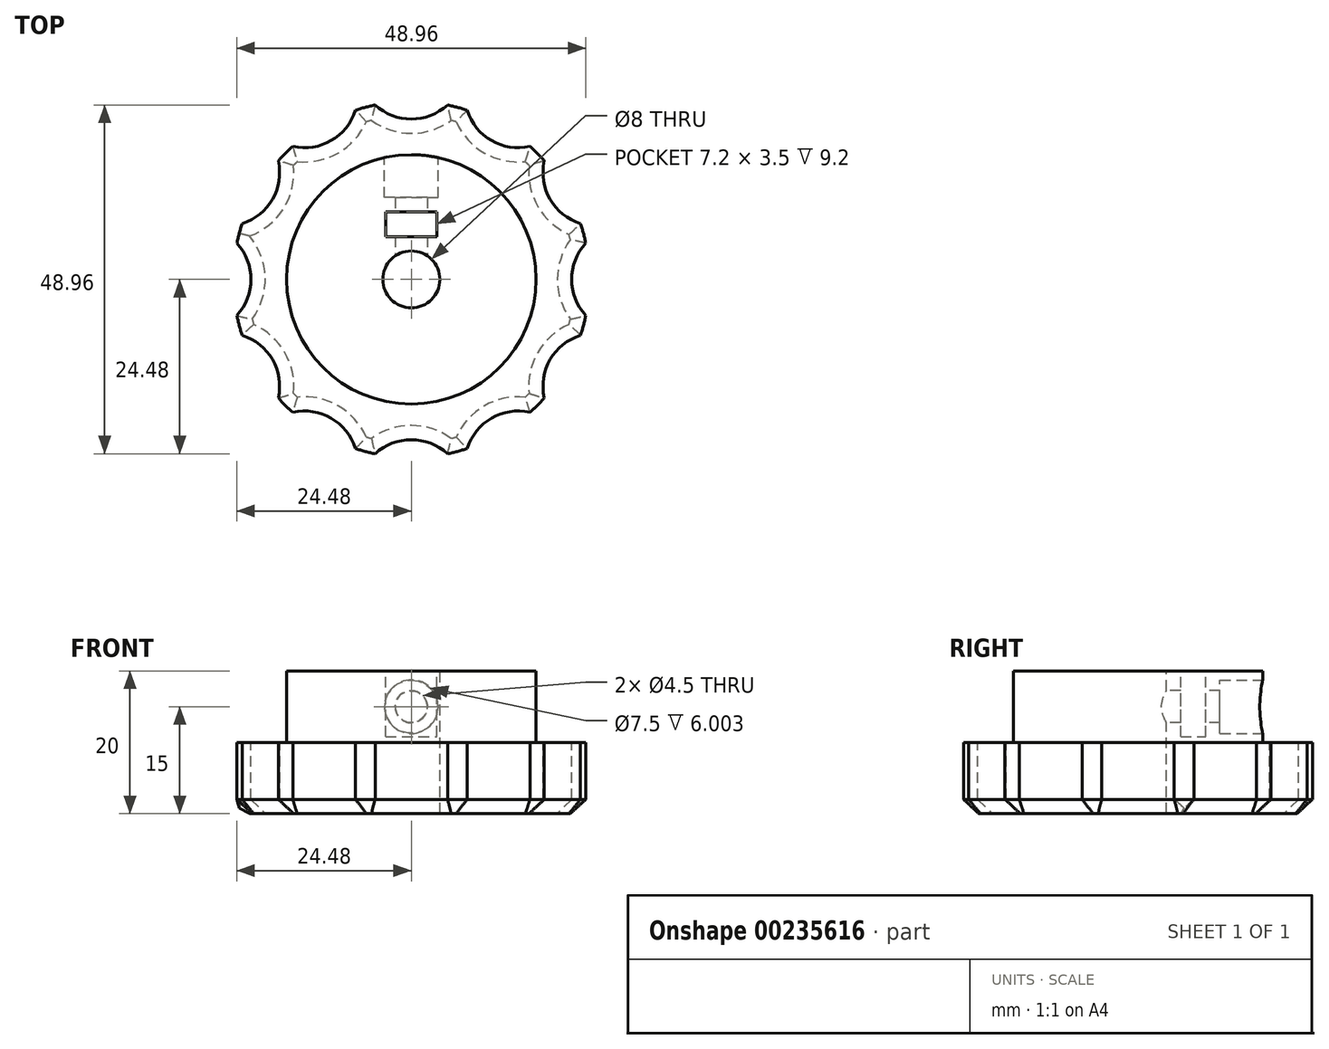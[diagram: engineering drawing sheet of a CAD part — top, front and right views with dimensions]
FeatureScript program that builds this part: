
annotation { "Feature Type Name" : "Feature", "Feature Type Description" : "" }
export const myFeature = defineFeature(function(context is Context, id is Id, definition is map)
    precondition{}
    {
        {
            var Q0;
            Q0=qCreatedBy(makeId("Top.planeOp"),FACE);
            var sketch = newSketch(context, id + "F0", { "sketchPlane" : qUnion([Q0])});
            skCircle(sketch, "E0", {"center": v(0, 0) * mm, "radius": 25 * mm});
            skSolve(sketch);
        }
        {
            var Q0;
            Q0 = qSketchRegion(id + "F0", true);
            extrude(context, id + "F1", {"entities" : qUnion([Q0]), "depth" : 10 * mm, "offsetDistance" : 25 * mm});
        }
        {
            var Q0;
            Q0=makeQuery(id+"F1.opExtrude","CAP_FACE",FACE,{"disambiguationData":[OSD([sQuery(id+"F0.wireOp",EDGE,"E0")])],"isStart":false});
            var sketch = newSketch(context, id + "F2", { "sketchPlane" : qUnion([Q0])});
            skCircle(sketch, "E1", {"center": v(0, 30) * mm, "radius": 7.5 * mm});
            skCircle(sketch, "E2.1.0", {"center": v(-15, 25.98) * mm, "radius": 7.5 * mm});
            skCircle(sketch, "E2.2.0", {"center": v(-25.98, 15) * mm, "radius": 7.5 * mm});
            skCircle(sketch, "E2.3.0", {"center": v(-30, 0) * mm, "radius": 7.5 * mm});
            skCircle(sketch, "E2.4.0", {"center": v(-25.98, -15) * mm, "radius": 7.5 * mm});
            skCircle(sketch, "E2.5.0", {"center": v(-15, -25.98) * mm, "radius": 7.5 * mm});
            skCircle(sketch, "E2.6.0", {"center": v(0, -30) * mm, "radius": 7.5 * mm});
            skCircle(sketch, "E2.7.0", {"center": v(15, -25.98) * mm, "radius": 7.5 * mm});
            skCircle(sketch, "E2.8.0", {"center": v(25.98, -15) * mm, "radius": 7.5 * mm});
            skCircle(sketch, "E2.9.0", {"center": v(30, 0) * mm, "radius": 7.5 * mm});
            skCircle(sketch, "E2.10.0", {"center": v(25.98, 15) * mm, "radius": 7.5 * mm});
            skCircle(sketch, "E2.11.0", {"center": v(15, 25.98) * mm, "radius": 7.5 * mm});
            skPoint(sketch, "E2.center", {"position": v(0, 0) * mm});
            skSolve(sketch);
        }
        {
            var Q0;
            Q0 = qSketchRegion(id + "F2", true);
            extrude(context, id + "F3", {"entities" : qUnion([Q0]), "operationType" : NewBodyOperationType.REMOVE, "endBound" : BoundingType.THROUGH_ALL, "oppositeDirection" : true, "depth" : 25 * mm, "offsetDistance" : 25 * mm});
        }
        {
            var Q0;
            Q0=makeQuery(id+"F1.opExtrude","CAP_FACE",FACE,{"disambiguationData":[OSD([sQuery(id+"F0.wireOp",EDGE,"E0")])],"isStart":false});
            var sketch = newSketch(context, id + "F4", { "sketchPlane" : qUnion([Q0])});
            skCircle(sketch, "E3", {"center": v(0, 0) * mm, "radius": 17.5 * mm});
            skSolve(sketch);
        }
        {
            var Q0;
            Q0=makeQuery(id+"F4.imprint","IMPRINT",FACE,{"disambiguationData":[TD([[makeQuery(id+"F4.imprint","IMPRINT",EDGE,{"derivedFrom":sQuery(id+"F4.wireOp",EDGE,"E3")}),1.0]])]});
            extrude(context, id + "F5", {"entities" : qUnion([Q0]), "operationType" : NewBodyOperationType.ADD, "depth" : 10 * mm, "offsetDistance" : 25 * mm});
        }
        {
            var Q0;
            Q0=makeQuery(id+"F5.opExtrude","CAP_FACE",FACE,{"disambiguationData":[OSD([sQuery(id+"F4.wireOp",EDGE,"E3")])],"isStart":false});
            var sketch = newSketch(context, id + "F6", { "sketchPlane" : qUnion([Q0])});
            skCircle(sketch, "E4", {"center": v(0, 0) * mm, "radius": 4 * mm});
            skSolve(sketch);
        }
        {
            var Q0;
            Q0 = qSketchRegion(id + "F6", true);
            extrude(context, id + "F7", {"entities" : qUnion([Q0]), "operationType" : NewBodyOperationType.REMOVE, "endBound" : BoundingType.UP_TO_NEXT, "oppositeDirection" : true, "depth" : 25 * mm, "offsetDistance" : 25 * mm});
        }
        {
            var Q0;
            Q0=qCreatedBy(makeId("Front.planeOp"),FACE);
            var sketch = newSketch(context, id + "F8", { "sketchPlane" : qUnion([Q0])});
            skCircle(sketch, "E5", {"center": v(0, 15) * mm, "radius": 2.25 * mm});
            skSolve(sketch);
        }
        {
            var Q0;
            Q0 = qSketchRegion(id + "F8", true);
            extrude(context, id + "F9", {"entities" : qUnion([Q0]), "operationType" : NewBodyOperationType.REMOVE, "endBound" : BoundingType.THROUGH_ALL, "oppositeDirection" : true, "depth" : 25 * mm, "offsetDistance" : 25 * mm});
        }
        {
            var Q0;
            Q0=makeQuery(id+"F5.opExtrude","CAP_FACE",FACE,{"disambiguationData":[OSD([sQuery(id+"F4.wireOp",EDGE,"E3")])],"isStart":false});
            var sketch = newSketch(context, id + "F10", { "sketchPlane" : qUnion([Q0])});
            skLineSegment(sketch, "E6.bottom", {"start": v(-3.6, 6) * mm, "end": v(3.6, 6) * mm});
            skLineSegment(sketch, "E6.top", {"start": v(-3.6, 9.5) * mm, "end": v(3.6, 9.5) * mm});
            skLineSegment(sketch, "E6.left", {"start": v(-3.6, 6) * mm, "end": v(-3.6, 9.5) * mm});
            skLineSegment(sketch, "E6.right", {"start": v(3.6, 6) * mm, "end": v(3.6, 9.5) * mm});
            skSolve(sketch);
        }
        {
            var Q0;
            Q0 = qSketchRegion(id + "F10", true);
            extrude(context, id + "F11", {"entities" : qUnion([Q0]), "operationType" : NewBodyOperationType.REMOVE, "oppositeDirection" : true, "depth" : 9.2 * mm, "offsetDistance" : 25 * mm});
        }
        {
            var Q0;
            Q0=qCreatedBy(makeId("Front.planeOp"),FACE);
            cPlane(context, id + "F12", {"entities" : qUnion([Q0]), "cplaneType" : CPlaneType.OFFSET, "offset" : 25 * mm, "oppositeDirection" : true, "width" : 150 * mm, "height" : 150 * mm});
        }
        {
            var Q0;
            Q0=qCreatedBy(id+"F12.planeOp",FACE);
            var sketch = newSketch(context, id + "F13", { "sketchPlane" : qUnion([Q0])});
            skCircle(sketch, "E7", {"center": v(0, 15) * mm, "radius": 3.75 * mm});
            skSolve(sketch);
        }
        {
            var Q0;
            Q0=makeQuery(id+"F13.imprint","IMPRINT",FACE,{"disambiguationData":[TD([[makeQuery(id+"F13.imprint","IMPRINT",EDGE,{"derivedFrom":sQuery(id+"F13.wireOp",EDGE,"E7")}),1.0]])]});
            var Q1;
            Q1=makeQuery(id+"F11.boolean.opBoolean","COPY",FACE,{"derivedFrom":makeQuery(id+"F11.opExtrude","SWEPT_FACE",FACE,{"disambiguationData":[OSD([sQuery(id+"F10.wireOp",EDGE,"E6.top")])]})});
            extrude(context, id + "F14", {"entities" : qUnion([Q0]), "operationType" : NewBodyOperationType.REMOVE, "endBound" : BoundingType.UP_TO_SURFACE, "depth" : 25 * mm, "endBoundEntityFace" : qUnion([Q1]), "hasOffset" : true, "offsetDistance" : 2 * mm});
        }
        {
            var Q0;
            Q0=makeQuery(id+"F3.boolean.opBoolean","INTERSECT",EDGE,{"derivedFrom":[makeQuery(id+"F1.opExtrude","CAP_FACE",FACE,{"disambiguationData":[OSD([sQuery(id+"F0.wireOp",EDGE,"E0")])],"isStart":true}),makeQuery(id+"F3.opExtrude","SWEPT_FACE",FACE,{"disambiguationData":[OSD([sQuery(id+"F2.wireOp",EDGE,"E2.10.0")])]})]});
            var Q1;
            {var subQ0=sQuery(id+"F0.wireOp",EDGE,"E0");Q1=makeQuery(id+"F3.boolean.opBoolean","SPLIT",EDGE,{"disambiguationData":[TD([makeQuery(id+"F1.opExtrude","SWEPT_FACE",FACE,{"disambiguationData":[OSD([subQ0])]}),makeQuery(id+"F1.opExtrude","CAP_FACE",FACE,{"disambiguationData":[OSD([subQ0])],"isStart":true}),makeQuery(id+"F3.opExtrude","SWEPT_FACE",FACE,{"disambiguationData":[OSD([sQuery(id+"F2.wireOp",EDGE,"E2.10.0")])]}),makeQuery(id+"F3.opExtrude","SWEPT_FACE",FACE,{"disambiguationData":[OSD([sQuery(id+"F2.wireOp",EDGE,"E2.11.0")])]})])],"derivedFrom":makeQuery(id+"F1.opExtrude","CAP_EDGE",EDGE,{"disambiguationData":[OSD([subQ0])],"isStart":true})});}
            var Q2;
            Q2=makeQuery(id+"F3.boolean.opBoolean","INTERSECT",EDGE,{"derivedFrom":[makeQuery(id+"F1.opExtrude","CAP_FACE",FACE,{"disambiguationData":[OSD([sQuery(id+"F0.wireOp",EDGE,"E0")])],"isStart":true}),makeQuery(id+"F3.opExtrude","SWEPT_FACE",FACE,{"disambiguationData":[OSD([sQuery(id+"F2.wireOp",EDGE,"E2.11.0")])]})]});
            var Q3;
            {var subQ0=sQuery(id+"F0.wireOp",EDGE,"E0");Q3=makeQuery(id+"F3.boolean.opBoolean","SPLIT",EDGE,{"disambiguationData":[TD([makeQuery(id+"F1.opExtrude","SWEPT_FACE",FACE,{"disambiguationData":[OSD([subQ0])]}),makeQuery(id+"F1.opExtrude","CAP_FACE",FACE,{"disambiguationData":[OSD([subQ0])],"isStart":true}),makeQuery(id+"F3.opExtrude","SWEPT_FACE",FACE,{"disambiguationData":[OSD([sQuery(id+"F2.wireOp",EDGE,"E1")])]}),makeQuery(id+"F3.opExtrude","SWEPT_FACE",FACE,{"disambiguationData":[OSD([sQuery(id+"F2.wireOp",EDGE,"E2.11.0")])]})])],"derivedFrom":makeQuery(id+"F1.opExtrude","CAP_EDGE",EDGE,{"disambiguationData":[OSD([subQ0])],"isStart":true})});}
            var Q4;
            Q4=makeQuery(id+"F3.boolean.opBoolean","INTERSECT",EDGE,{"derivedFrom":[makeQuery(id+"F1.opExtrude","CAP_FACE",FACE,{"disambiguationData":[OSD([sQuery(id+"F0.wireOp",EDGE,"E0")])],"isStart":true}),makeQuery(id+"F3.opExtrude","SWEPT_FACE",FACE,{"disambiguationData":[OSD([sQuery(id+"F2.wireOp",EDGE,"E1")])]})]});
            var Q5;
            {var subQ0=sQuery(id+"F0.wireOp",EDGE,"E0");Q5=makeQuery(id+"F3.boolean.opBoolean","SPLIT",EDGE,{"disambiguationData":[TD([makeQuery(id+"F1.opExtrude","SWEPT_FACE",FACE,{"disambiguationData":[OSD([subQ0])]}),makeQuery(id+"F1.opExtrude","CAP_FACE",FACE,{"disambiguationData":[OSD([subQ0])],"isStart":true}),makeQuery(id+"F3.opExtrude","SWEPT_FACE",FACE,{"disambiguationData":[OSD([sQuery(id+"F2.wireOp",EDGE,"E1")])]}),makeQuery(id+"F3.opExtrude","SWEPT_FACE",FACE,{"disambiguationData":[OSD([sQuery(id+"F2.wireOp",EDGE,"E2.1.0")])]})])],"derivedFrom":makeQuery(id+"F1.opExtrude","CAP_EDGE",EDGE,{"disambiguationData":[OSD([subQ0])],"isStart":true})});}
            var Q6;
            Q6=makeQuery(id+"F3.boolean.opBoolean","INTERSECT",EDGE,{"derivedFrom":[makeQuery(id+"F1.opExtrude","CAP_FACE",FACE,{"disambiguationData":[OSD([sQuery(id+"F0.wireOp",EDGE,"E0")])],"isStart":true}),makeQuery(id+"F3.opExtrude","SWEPT_FACE",FACE,{"disambiguationData":[OSD([sQuery(id+"F2.wireOp",EDGE,"E2.1.0")])]})]});
            var Q7;
            {var subQ0=sQuery(id+"F0.wireOp",EDGE,"E0");Q7=makeQuery(id+"F3.boolean.opBoolean","SPLIT",EDGE,{"disambiguationData":[TD([makeQuery(id+"F1.opExtrude","SWEPT_FACE",FACE,{"disambiguationData":[OSD([subQ0])]}),makeQuery(id+"F1.opExtrude","CAP_FACE",FACE,{"disambiguationData":[OSD([subQ0])],"isStart":true}),makeQuery(id+"F3.opExtrude","SWEPT_FACE",FACE,{"disambiguationData":[OSD([sQuery(id+"F2.wireOp",EDGE,"E2.1.0")])]}),makeQuery(id+"F3.opExtrude","SWEPT_FACE",FACE,{"disambiguationData":[OSD([sQuery(id+"F2.wireOp",EDGE,"E2.2.0")])]})])],"derivedFrom":makeQuery(id+"F1.opExtrude","CAP_EDGE",EDGE,{"disambiguationData":[OSD([subQ0])],"isStart":true})});}
            var Q8;
            Q8=makeQuery(id+"F3.boolean.opBoolean","INTERSECT",EDGE,{"derivedFrom":[makeQuery(id+"F1.opExtrude","CAP_FACE",FACE,{"disambiguationData":[OSD([sQuery(id+"F0.wireOp",EDGE,"E0")])],"isStart":true}),makeQuery(id+"F3.opExtrude","SWEPT_FACE",FACE,{"disambiguationData":[OSD([sQuery(id+"F2.wireOp",EDGE,"E2.2.0")])]})]});
            var Q9;
            Q9=makeQuery(id+"F3.boolean.opBoolean","INTERSECT",EDGE,{"derivedFrom":[makeQuery(id+"F1.opExtrude","CAP_FACE",FACE,{"disambiguationData":[OSD([sQuery(id+"F0.wireOp",EDGE,"E0")])],"isStart":true}),makeQuery(id+"F3.opExtrude","SWEPT_FACE",FACE,{"disambiguationData":[OSD([sQuery(id+"F2.wireOp",EDGE,"E2.3.0")])]})]});
            var Q10;
            {var subQ0=sQuery(id+"F0.wireOp",EDGE,"E0");Q10=makeQuery(id+"F3.boolean.opBoolean","SPLIT",EDGE,{"disambiguationData":[TD([makeQuery(id+"F1.opExtrude","SWEPT_FACE",FACE,{"disambiguationData":[OSD([subQ0])]}),makeQuery(id+"F1.opExtrude","CAP_FACE",FACE,{"disambiguationData":[OSD([subQ0])],"isStart":true}),makeQuery(id+"F3.opExtrude","SWEPT_FACE",FACE,{"disambiguationData":[OSD([sQuery(id+"F2.wireOp",EDGE,"E2.3.0")])]}),makeQuery(id+"F3.opExtrude","SWEPT_FACE",FACE,{"disambiguationData":[OSD([sQuery(id+"F2.wireOp",EDGE,"E2.4.0")])]})])],"derivedFrom":makeQuery(id+"F1.opExtrude","CAP_EDGE",EDGE,{"disambiguationData":[OSD([subQ0])],"isStart":true})});}
            var Q11;
            Q11=makeQuery(id+"F3.boolean.opBoolean","INTERSECT",EDGE,{"derivedFrom":[makeQuery(id+"F1.opExtrude","CAP_FACE",FACE,{"disambiguationData":[OSD([sQuery(id+"F0.wireOp",EDGE,"E0")])],"isStart":true}),makeQuery(id+"F3.opExtrude","SWEPT_FACE",FACE,{"disambiguationData":[OSD([sQuery(id+"F2.wireOp",EDGE,"E2.4.0")])]})]});
            var Q12;
            {var subQ0=sQuery(id+"F0.wireOp",EDGE,"E0");Q12=makeQuery(id+"F3.boolean.opBoolean","SPLIT",EDGE,{"disambiguationData":[TD([makeQuery(id+"F1.opExtrude","SWEPT_FACE",FACE,{"disambiguationData":[OSD([subQ0])]}),makeQuery(id+"F1.opExtrude","CAP_FACE",FACE,{"disambiguationData":[OSD([subQ0])],"isStart":true}),makeQuery(id+"F3.opExtrude","SWEPT_FACE",FACE,{"disambiguationData":[OSD([sQuery(id+"F2.wireOp",EDGE,"E2.4.0")])]}),makeQuery(id+"F3.opExtrude","SWEPT_FACE",FACE,{"disambiguationData":[OSD([sQuery(id+"F2.wireOp",EDGE,"E2.5.0")])]})])],"derivedFrom":makeQuery(id+"F1.opExtrude","CAP_EDGE",EDGE,{"disambiguationData":[OSD([subQ0])],"isStart":true})});}
            var Q13;
            Q13=makeQuery(id+"F3.boolean.opBoolean","INTERSECT",EDGE,{"derivedFrom":[makeQuery(id+"F1.opExtrude","CAP_FACE",FACE,{"disambiguationData":[OSD([sQuery(id+"F0.wireOp",EDGE,"E0")])],"isStart":true}),makeQuery(id+"F3.opExtrude","SWEPT_FACE",FACE,{"disambiguationData":[OSD([sQuery(id+"F2.wireOp",EDGE,"E2.5.0")])]})]});
            var Q14;
            {var subQ0=sQuery(id+"F0.wireOp",EDGE,"E0");Q14=makeQuery(id+"F3.boolean.opBoolean","SPLIT",EDGE,{"disambiguationData":[TD([makeQuery(id+"F1.opExtrude","SWEPT_FACE",FACE,{"disambiguationData":[OSD([subQ0])]}),makeQuery(id+"F1.opExtrude","CAP_FACE",FACE,{"disambiguationData":[OSD([subQ0])],"isStart":true}),makeQuery(id+"F3.opExtrude","SWEPT_FACE",FACE,{"disambiguationData":[OSD([sQuery(id+"F2.wireOp",EDGE,"E2.5.0")])]}),makeQuery(id+"F3.opExtrude","SWEPT_FACE",FACE,{"disambiguationData":[OSD([sQuery(id+"F2.wireOp",EDGE,"E2.6.0")])]})])],"derivedFrom":makeQuery(id+"F1.opExtrude","CAP_EDGE",EDGE,{"disambiguationData":[OSD([subQ0])],"isStart":true})});}
            var Q15;
            Q15=makeQuery(id+"F3.boolean.opBoolean","INTERSECT",EDGE,{"derivedFrom":[makeQuery(id+"F1.opExtrude","CAP_FACE",FACE,{"disambiguationData":[OSD([sQuery(id+"F0.wireOp",EDGE,"E0")])],"isStart":true}),makeQuery(id+"F3.opExtrude","SWEPT_FACE",FACE,{"disambiguationData":[OSD([sQuery(id+"F2.wireOp",EDGE,"E2.6.0")])]})]});
            var Q16;
            {var subQ0=sQuery(id+"F0.wireOp",EDGE,"E0");Q16=makeQuery(id+"F3.boolean.opBoolean","SPLIT",EDGE,{"disambiguationData":[TD([makeQuery(id+"F1.opExtrude","SWEPT_FACE",FACE,{"disambiguationData":[OSD([subQ0])]}),makeQuery(id+"F1.opExtrude","CAP_FACE",FACE,{"disambiguationData":[OSD([subQ0])],"isStart":true}),makeQuery(id+"F3.opExtrude","SWEPT_FACE",FACE,{"disambiguationData":[OSD([sQuery(id+"F2.wireOp",EDGE,"E2.6.0")])]}),makeQuery(id+"F3.opExtrude","SWEPT_FACE",FACE,{"disambiguationData":[OSD([sQuery(id+"F2.wireOp",EDGE,"E2.7.0")])]})])],"derivedFrom":makeQuery(id+"F1.opExtrude","CAP_EDGE",EDGE,{"disambiguationData":[OSD([subQ0])],"isStart":true})});}
            var Q17;
            Q17=makeQuery(id+"F3.boolean.opBoolean","INTERSECT",EDGE,{"derivedFrom":[makeQuery(id+"F1.opExtrude","CAP_FACE",FACE,{"disambiguationData":[OSD([sQuery(id+"F0.wireOp",EDGE,"E0")])],"isStart":true}),makeQuery(id+"F3.opExtrude","SWEPT_FACE",FACE,{"disambiguationData":[OSD([sQuery(id+"F2.wireOp",EDGE,"E2.7.0")])]})]});
            var Q18;
            {var subQ0=sQuery(id+"F0.wireOp",EDGE,"E0");Q18=makeQuery(id+"F3.boolean.opBoolean","SPLIT",EDGE,{"disambiguationData":[TD([makeQuery(id+"F1.opExtrude","SWEPT_FACE",FACE,{"disambiguationData":[OSD([subQ0])]}),makeQuery(id+"F1.opExtrude","CAP_FACE",FACE,{"disambiguationData":[OSD([subQ0])],"isStart":true}),makeQuery(id+"F3.opExtrude","SWEPT_FACE",FACE,{"disambiguationData":[OSD([sQuery(id+"F2.wireOp",EDGE,"E2.7.0")])]}),makeQuery(id+"F3.opExtrude","SWEPT_FACE",FACE,{"disambiguationData":[OSD([sQuery(id+"F2.wireOp",EDGE,"E2.8.0")])]})])],"derivedFrom":makeQuery(id+"F1.opExtrude","CAP_EDGE",EDGE,{"disambiguationData":[OSD([subQ0])],"isStart":true})});}
            var Q19;
            Q19=makeQuery(id+"F3.boolean.opBoolean","INTERSECT",EDGE,{"derivedFrom":[makeQuery(id+"F1.opExtrude","CAP_FACE",FACE,{"disambiguationData":[OSD([sQuery(id+"F0.wireOp",EDGE,"E0")])],"isStart":true}),makeQuery(id+"F3.opExtrude","SWEPT_FACE",FACE,{"disambiguationData":[OSD([sQuery(id+"F2.wireOp",EDGE,"E2.8.0")])]})]});
            var Q20;
            {var subQ0=sQuery(id+"F0.wireOp",EDGE,"E0");Q20=makeQuery(id+"F3.boolean.opBoolean","SPLIT",EDGE,{"disambiguationData":[TD([makeQuery(id+"F1.opExtrude","SWEPT_FACE",FACE,{"disambiguationData":[OSD([subQ0])]}),makeQuery(id+"F1.opExtrude","CAP_FACE",FACE,{"disambiguationData":[OSD([subQ0])],"isStart":true}),makeQuery(id+"F3.opExtrude","SWEPT_FACE",FACE,{"disambiguationData":[OSD([sQuery(id+"F2.wireOp",EDGE,"E2.8.0")])]}),makeQuery(id+"F3.opExtrude","SWEPT_FACE",FACE,{"disambiguationData":[OSD([sQuery(id+"F2.wireOp",EDGE,"E2.9.0")])]})])],"derivedFrom":makeQuery(id+"F1.opExtrude","CAP_EDGE",EDGE,{"disambiguationData":[OSD([subQ0])],"isStart":true})});}
            var Q21;
            Q21=makeQuery(id+"F3.boolean.opBoolean","INTERSECT",EDGE,{"derivedFrom":[makeQuery(id+"F1.opExtrude","CAP_FACE",FACE,{"disambiguationData":[OSD([sQuery(id+"F0.wireOp",EDGE,"E0")])],"isStart":true}),makeQuery(id+"F3.opExtrude","SWEPT_FACE",FACE,{"disambiguationData":[OSD([sQuery(id+"F2.wireOp",EDGE,"E2.9.0")])]})]});
            var Q22;
            {var subQ0=sQuery(id+"F0.wireOp",EDGE,"E0");Q22=makeQuery(id+"F3.boolean.opBoolean","SPLIT",EDGE,{"disambiguationData":[TD([makeQuery(id+"F1.opExtrude","SWEPT_FACE",FACE,{"disambiguationData":[OSD([subQ0])]}),makeQuery(id+"F1.opExtrude","CAP_FACE",FACE,{"disambiguationData":[OSD([subQ0])],"isStart":true}),makeQuery(id+"F3.opExtrude","SWEPT_FACE",FACE,{"disambiguationData":[OSD([sQuery(id+"F2.wireOp",EDGE,"E2.9.0")])]}),makeQuery(id+"F3.opExtrude","SWEPT_FACE",FACE,{"disambiguationData":[OSD([sQuery(id+"F2.wireOp",EDGE,"E2.10.0")])]})])],"derivedFrom":makeQuery(id+"F1.opExtrude","CAP_EDGE",EDGE,{"disambiguationData":[OSD([subQ0])],"isStart":true})});}
            chamfer(context, id + "F15", {"entities" : qUnion([Q0, Q1, Q2, Q3, Q4, Q5, Q6, Q7, Q8, Q9, Q10, Q11, Q12, Q13, Q14, Q15, Q16, Q17, Q18, Q19, Q20, Q21, Q22]), "width" : 2 * mm, "tangentPropagation" : true});
        }
    });
